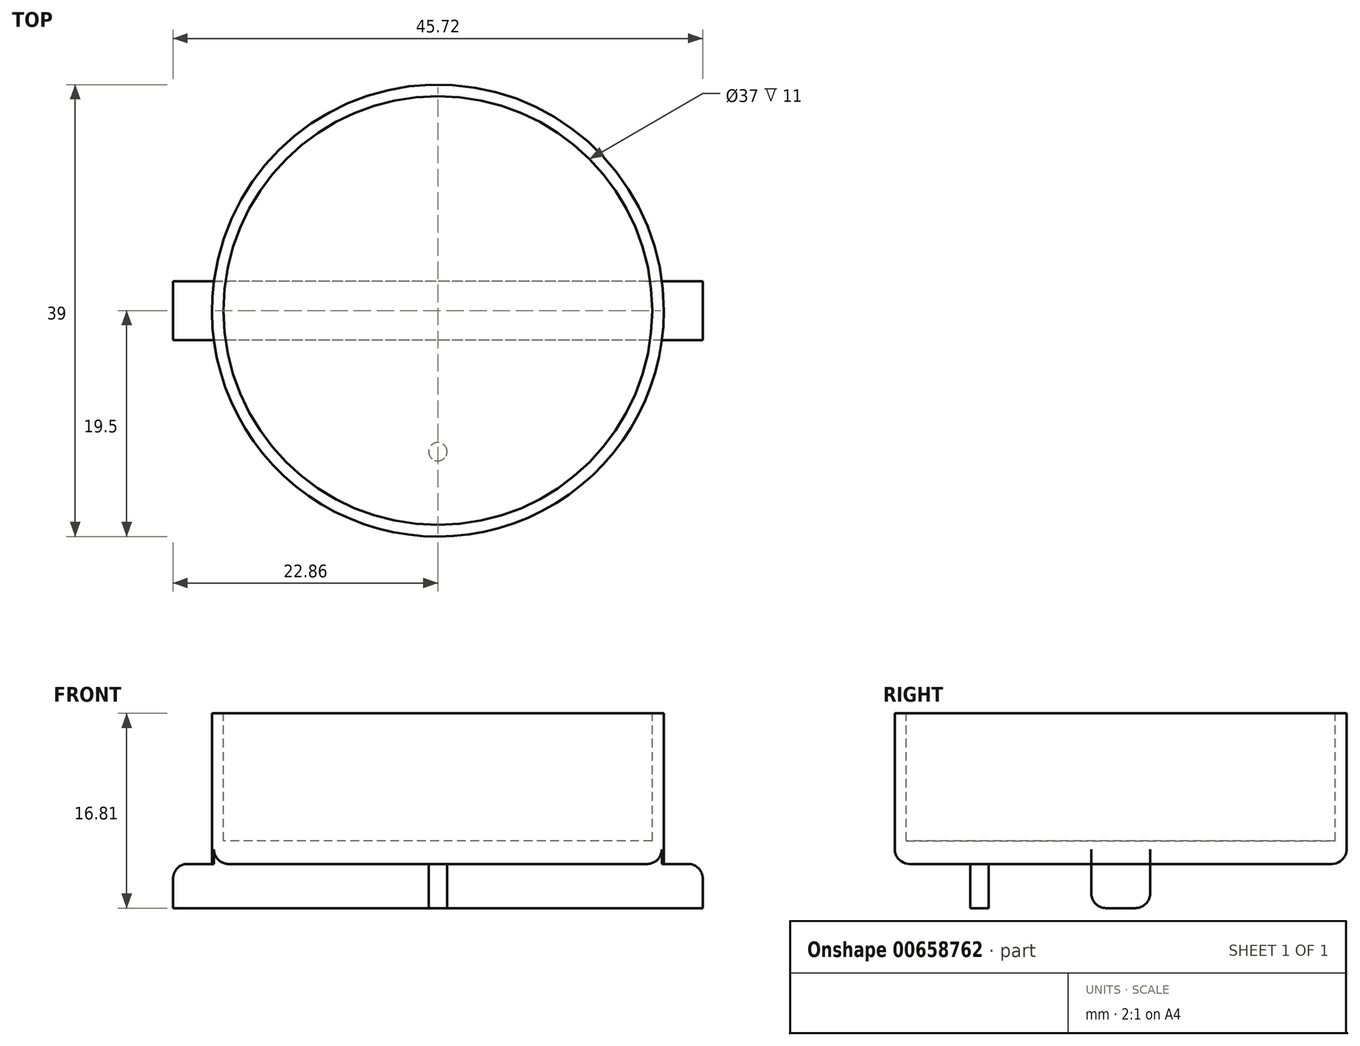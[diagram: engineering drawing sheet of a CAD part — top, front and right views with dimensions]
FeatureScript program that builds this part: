
annotation { "Feature Type Name" : "Feature", "Feature Type Description" : "" }
export const myFeature = defineFeature(function(context is Context, id is Id, definition is map)
    precondition{}
    {
        {
            var Q0;
            Q0=qCreatedBy(makeId("Top.planeOp"),FACE);
            var sketch = newSketch(context, id + "F0", { "sketchPlane" : qUnion([Q0])});
            skCircle(sketch, "E0", {"center": v(0, 0) * mm, "radius": 19.5 * mm});
            skSolve(sketch);
        }
        {
            var Q0;
            Q0 = qSketchRegion(id + "F0", true);
            extrude(context, id + "F1", {"entities" : qUnion([Q0]), "depth" : 13 * mm, "offsetDistance" : 25.4 * mm});
        }
        {
            var Q0;
            Q0=makeQuery(id+"F1.opExtrude","CAP_FACE",FACE,{"disambiguationData":[OSD([sQuery(id+"F0.wireOp",EDGE,"E0")])],"isStart":false});
            var sketch = newSketch(context, id + "F2", { "sketchPlane" : qUnion([Q0])});
            skCircle(sketch, "E1", {"center": v(0, 0) * mm, "radius": 18.5 * mm});
            skSolve(sketch);
        }
        {
            var Q0;
            Q0 = qSketchRegion(id + "F2", true);
            extrude(context, id + "F3", {"entities" : qUnion([Q0]), "operationType" : NewBodyOperationType.REMOVE, "oppositeDirection" : true, "depth" : 11 * mm, "offsetDistance" : 25.4 * mm});
        }
        {
            var Q0;
            Q0=makeQuery(id+"F1.opExtrude","CAP_FACE",FACE,{"disambiguationData":[OSD([sQuery(id+"F0.wireOp",EDGE,"E0")])],"isStart":true});
            var sketch = newSketch(context, id + "F4", { "sketchPlane" : qUnion([Q0])});
            skLineSegment(sketch, "E2.bottom", {"start": v(22.86, 2.54) * mm, "end": v(-22.86, 2.54) * mm});
            skLineSegment(sketch, "E2.top", {"start": v(22.86, -2.54) * mm, "end": v(-22.86, -2.54) * mm});
            skLineSegment(sketch, "E2.left", {"start": v(22.86, 2.54) * mm, "end": v(22.86, -2.54) * mm});
            skLineSegment(sketch, "E2.right", {"start": v(-22.86, 2.54) * mm, "end": v(-22.86, -2.54) * mm});
            skPoint(sketch, "E2.middle", {"position": v(0, 0) * mm});
            skSolve(sketch);
        }
        {
            var Q0;
            Q0 = qSketchRegion(id + "F4", true);
            extrude(context, id + "F5", {"entities" : qUnion([Q0]), "operationType" : NewBodyOperationType.ADD, "depth" : 3.8 * mm, "offsetDistance" : 25.4 * mm});
        }
        {
            var Q0;
            Q0=makeQuery(id+"F5.opExtrude","CAP_EDGE",EDGE,{"disambiguationData":[OSD([sQuery(id+"F4.wireOp",EDGE,"E2.bottom")])],"isStart":false});
            var Q1;
            Q1=makeQuery(id+"F5.opExtrude","CAP_EDGE",EDGE,{"disambiguationData":[OSD([sQuery(id+"F4.wireOp",EDGE,"E2.top")])],"isStart":false});
            var Q2;
            {var subQ0=sQuery(id+"F0.wireOp",EDGE,"E0");var subQ1=makeQuery(id+"F1.opExtrude","SWEPT_FACE",FACE,{"disambiguationData":[OSD([subQ0])]});var subQ2=makeQuery(id+"F1.opExtrude","CAP_FACE",FACE,{"disambiguationData":[OSD([subQ0])],"isStart":true});var subQ3=sQuery(id+"F4.wireOp",EDGE,"E2.bottom");Q2=makeQuery(id+"F5.boolean.opBoolean","SPLIT",EDGE,{"disambiguationData":[topologyDisambiguationEdgeConnected([subQ1,subQ2]),TD([makeQuery(id+"F5.opExtrude","SWEPT_FACE",FACE,{"disambiguationData":[OSD([subQ3])]})])],"derivedFrom":makeQuery(id+"F1.opExtrude","CAP_EDGE",EDGE,{"disambiguationData":[OSD([subQ0])],"isStart":true})});}
            var Q3;
            {var subQ0=sQuery(id+"F0.wireOp",EDGE,"E0");var subQ1=makeQuery(id+"F1.opExtrude","SWEPT_FACE",FACE,{"disambiguationData":[OSD([subQ0])]});var subQ2=sQuery(id+"F4.wireOp",EDGE,"E2.top");var subQ3=makeQuery(id+"F1.opExtrude","CAP_FACE",FACE,{"disambiguationData":[OSD([subQ0])],"isStart":true});Q3=makeQuery(id+"F5.boolean.opBoolean","SPLIT",EDGE,{"disambiguationData":[topologyDisambiguationEdgeConnected([subQ1,subQ3]),TD([makeQuery(id+"F5.opExtrude","SWEPT_FACE",FACE,{"disambiguationData":[OSD([subQ2])]})])],"derivedFrom":makeQuery(id+"F1.opExtrude","CAP_EDGE",EDGE,{"disambiguationData":[OSD([subQ0])],"isStart":true})});}
            var Q4;
            Q4=makeQuery(id+"F5.opExtrude","CAP_EDGE",EDGE,{"disambiguationData":[OSD([sQuery(id+"F4.wireOp",EDGE,"E2.right")])],"isStart":true});
            var Q5;
            Q5=makeQuery(id+"F5.opExtrude","CAP_EDGE",EDGE,{"disambiguationData":[OSD([sQuery(id+"F4.wireOp",EDGE,"E2.left")])],"isStart":true});
            fillet(context, id + "F6", {"entities" : qUnion([Q0, Q1, Q2, Q3, Q4, Q5]), "radius" : 1.27 * mm, "tangentPropagation" : true, "allowEdgeOverflow" : false});
        }
        {
            var Q0;
            {var subQ0=sQuery(id+"F0.wireOp",EDGE,"E0");var subQ1=sQuery(id+"F4.wireOp",EDGE,"E2.bottom");Q0=makeQuery(id+"F5.boolean.opBoolean","SPLIT",FACE,{"disambiguationData":[TD([makeQuery(id+"F5.opExtrude","SWEPT_FACE",FACE,{"disambiguationData":[OSD([subQ1])]})])],"derivedFrom":makeQuery(id+"F1.opExtrude","CAP_FACE",FACE,{"disambiguationData":[OSD([subQ0])],"isStart":true})});}
            var sketch = newSketch(context, id + "F7", { "sketchPlane" : qUnion([Q0])});
            skCircle(sketch, "E3", {"center": v(0, 12.18) * mm, "radius": 0.8 * mm});
            skCircle(sketch, "E4.1.0", {"center": v(-10.55, -6.09) * mm, "radius": 0.8 * mm});
            skCircle(sketch, "E4.2.0", {"center": v(10.55, -6.09) * mm, "radius": 0.8 * mm});
            skPoint(sketch, "E4.center", {"position": v(0, 0) * mm});
            skLineSegment(sketch, "E5.anchor1", {"start": v(0, 0) * mm, "end": v(0, 12.18) * mm, "construction": true});
            skLineSegment(sketch, "E5.anchor2", {"start": v(0, 0) * mm, "end": v(-10.55, -6.09) * mm, "construction": true});
            skSolve(sketch);
        }
        {
            var Q0;
            Q0=makeQuery(id+"F7.imprint","IMPRINT",FACE,{"disambiguationData":[TD([[makeQuery(id+"F7.imprint","IMPRINT",EDGE,{"derivedFrom":sQuery(id+"F7.wireOp",EDGE,"E4.2.0")}),1.0]])]});
            var Q1;
            Q1=makeQuery(id+"F7.imprint","IMPRINT",FACE,{"disambiguationData":[TD([[makeQuery(id+"F7.imprint","IMPRINT",EDGE,{"derivedFrom":sQuery(id+"F7.wireOp",EDGE,"E4.1.0")}),1.0]])]});
            var Q2;
            Q2=makeQuery(id+"F7.imprint","IMPRINT",FACE,{"disambiguationData":[TD([[makeQuery(id+"F7.imprint","IMPRINT",EDGE,{"derivedFrom":sQuery(id+"F7.wireOp",EDGE,"E3")}),1.0]])]});
            var Q3;
            Q3=makeQuery(id+"F5.opExtrude","CAP_FACE",FACE,{"disambiguationData":[OSD([sQuery(id+"F4.wireOp",EDGE,"E2.bottom"),sQuery(id+"F4.wireOp",EDGE,"E2.top"),sQuery(id+"F4.wireOp",EDGE,"E2.left"),sQuery(id+"F4.wireOp",EDGE,"E2.right")])],"isStart":false});
            extrude(context, id + "F8", {"entities" : qUnion([Q0, Q1, Q2]), "operationType" : NewBodyOperationType.ADD, "endBound" : BoundingType.UP_TO_SURFACE, "depth" : 25.4 * mm, "endBoundEntityFace" : qUnion([Q3]), "offsetDistance" : 25.4 * mm});
        }
    });
